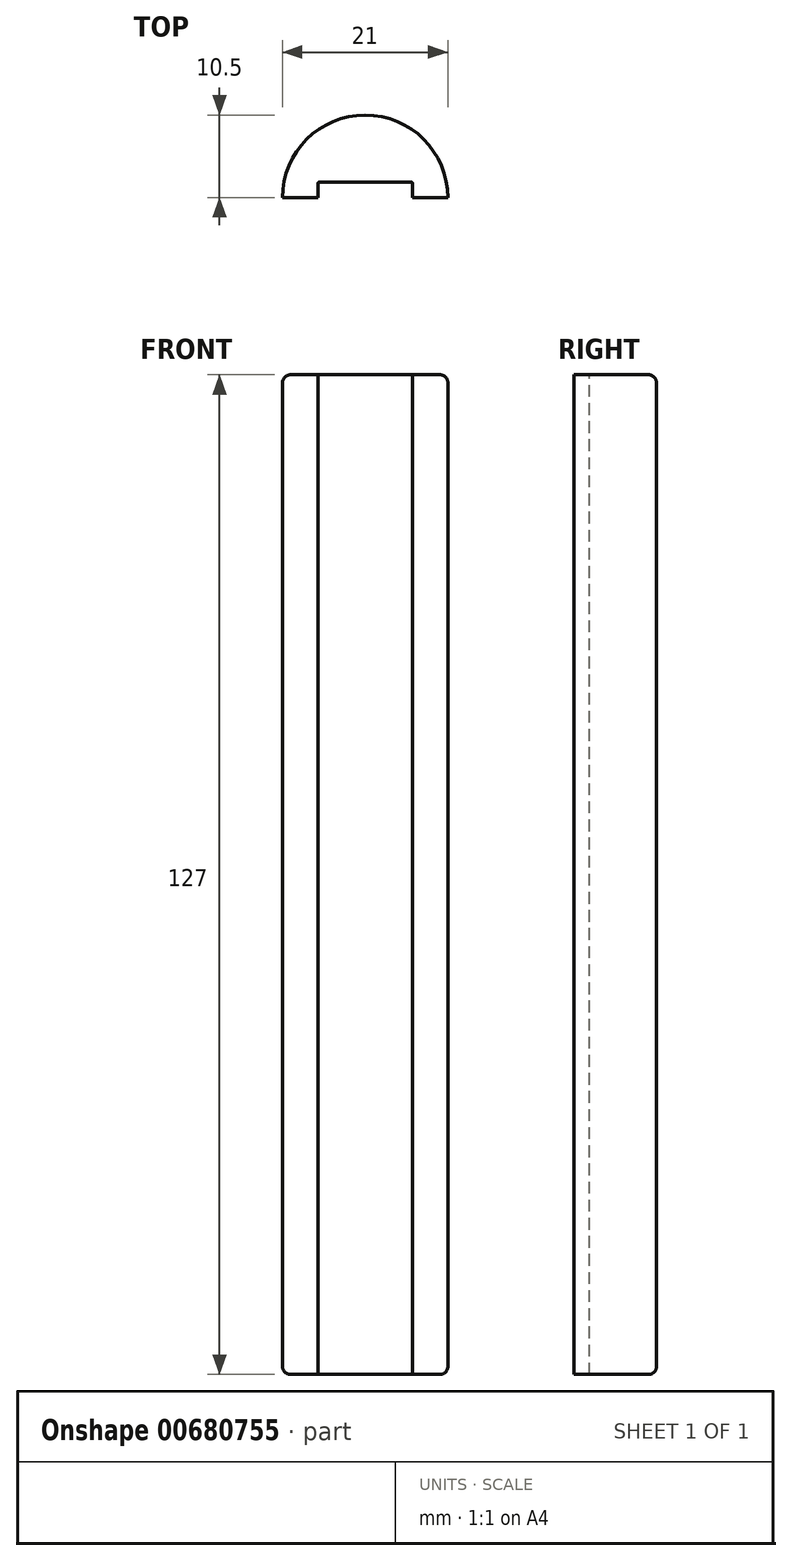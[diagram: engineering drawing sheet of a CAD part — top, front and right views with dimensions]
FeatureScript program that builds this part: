
annotation { "Feature Type Name" : "Feature", "Feature Type Description" : "" }
export const myFeature = defineFeature(function(context is Context, id is Id, definition is map)
    precondition{}
    {
        {
            var Q0;
            Q0=qCreatedBy(makeId("Front.planeOp"),FACE);
            var sketch = newSketch(context, id + "F0", { "sketchPlane" : qUnion([Q0])});
            skLineSegment(sketch, "E0.bottom", {"start": v(-5.25, 63.5) * mm, "end": v(5.25, 63.5) * mm});
            skLineSegment(sketch, "E0.top", {"start": v(-5.25, -63.5) * mm, "end": v(5.25, -63.5) * mm});
            skLineSegment(sketch, "E0.left", {"start": v(-5.25, 63.5) * mm, "end": v(-5.25, -63.5) * mm});
            skLineSegment(sketch, "E0.right", {"start": v(5.25, 63.5) * mm, "end": v(5.25, -63.5) * mm});
            skPoint(sketch, "E0.middle", {"position": v(0, 0) * mm});
            skSolve(sketch);
        }
        {
            var Q0;
            Q0=makeQuery(id+"F0.imprint","IMPRINT",FACE,{"disambiguationData":[TD([[makeQuery(id+"F0.imprint","IMPRINT",EDGE,{"derivedFrom":sQuery(id+"F0.wireOp",EDGE,"E0.bottom")}),-1.0]])]});
            var Q1;
            Q1=sQuery(id+"F0.wireOp",EDGE,"E0.right");
            revolve(context, id + "F1", {"entities" : qUnion([Q0]), "axis" : qUnion([Q1]), "revolveType" : RevolveType.ONE_DIRECTION, "angle" : 180 * degree});
        }
        {
            var Q0;
            Q0=makeQuery(id+"F1.opRevolve","SWEPT_FACE",FACE,{"disambiguationData":[OSD([sQuery(id+"F0.wireOp",EDGE,"E0.bottom")])]});
            var sketch = newSketch(context, id + "F2", { "sketchPlane" : qUnion([Q0])});
            skLineSegment(sketch, "E1", {"start": v(5.25, 0) * mm, "end": v(11.25, 0) * mm});
            skLineSegment(sketch, "E2", {"start": v(5.25, 0) * mm, "end": v(-0.75, 0) * mm});
            skLineSegment(sketch, "E3", {"start": v(-0.75, 0) * mm, "end": v(-0.75, 1.8) * mm});
            skLineSegment(sketch, "E4", {"start": v(-0.55, 2) * mm, "end": v(11.05, 2) * mm});
            skLineSegment(sketch, "E5", {"start": v(11.25, 1.8) * mm, "end": v(11.25, 0) * mm});
            skPoint(sketch, "E6.visualSharp", {"position": v(-0.75, 2) * mm});
            skArc(sketch, "E6.filletArc", {"start": v(-0.55, 2) * mm, "mid": v(-0.7, 1.94) * mm, "end": v(-0.75, 1.8) * mm});
            skPoint(sketch, "E7.visualSharp", {"position": v(11.25, 2) * mm});
            skArc(sketch, "E7.filletArc", {"start": v(11.25, 1.8) * mm, "mid": v(11.2, 1.94) * mm, "end": v(11.05, 2) * mm});
            skSolve(sketch);
        }
        {
            var Q0;
            Q0=makeQuery(id+"F2.imprint","IMPRINT",FACE,{"disambiguationData":[TD([[makeQuery(id+"F2.imprint","IMPRINT",EDGE,{"derivedFrom":sQuery(id+"F2.wireOp",EDGE,"E1")}),-1.0]])]});
            extrude(context, id + "F3", {"entities" : qUnion([Q0]), "operationType" : NewBodyOperationType.REMOVE, "oppositeDirection" : true, "depth" : 127 * mm, "offsetDistance" : 25 * mm});
        }
        {
            var Q0;
            Q0=makeQuery(id+"F1.opRevolve","SWEPT_EDGE",EDGE,{"disambiguationData":[OSD([sQuery(id+"F0.wireOp",EDGE,"E0.bottom"),sQuery(id+"F0.wireOp",EDGE,"E0.left")])]});
            fillet(context, id + "F4", {"entities" : qUnion([Q0]), "radius" : 1 * mm, "tangentPropagation" : true, "allowEdgeOverflow" : false});
        }
        {
            var Q0;
            Q0=makeQuery(id+"F1.opRevolve","SWEPT_EDGE",EDGE,{"disambiguationData":[OSD([sQuery(id+"F0.wireOp",EDGE,"E0.top"),sQuery(id+"F0.wireOp",EDGE,"E0.left")])]});
            fillet(context, id + "F5", {"entities" : qUnion([Q0]), "radius" : 1 * mm, "tangentPropagation" : true, "allowEdgeOverflow" : false});
        }
    });
